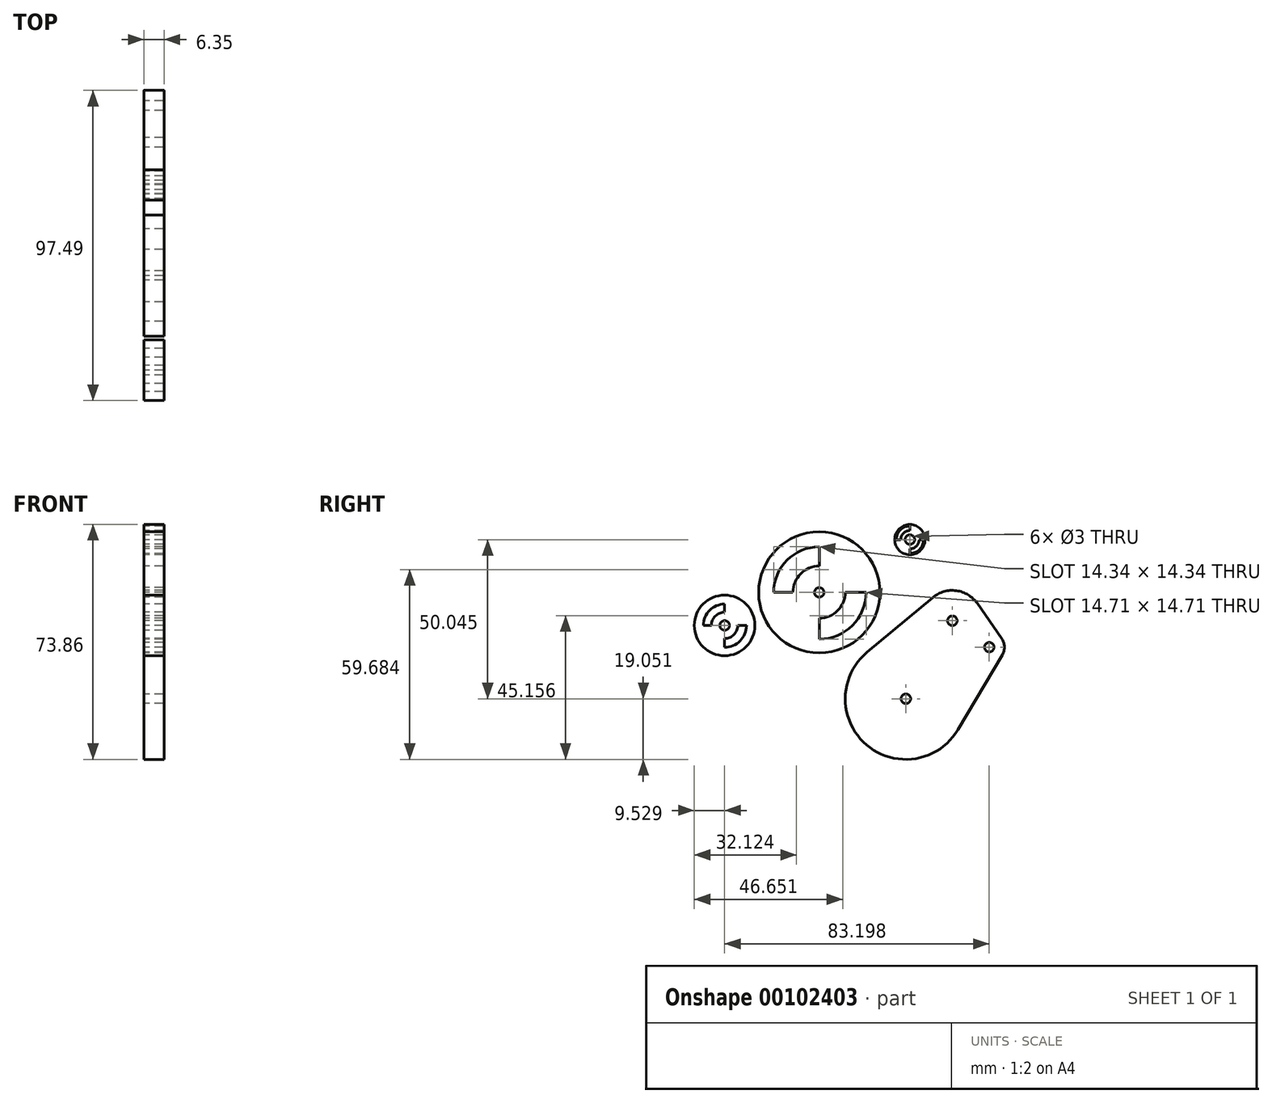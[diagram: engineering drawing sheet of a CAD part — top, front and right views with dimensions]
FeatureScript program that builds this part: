
annotation { "Feature Type Name" : "Feature", "Feature Type Description" : "" }
export const myFeature = defineFeature(function(context is Context, id is Id, definition is map)
    precondition{}
    {
        {
            var Q0;
            Q0=qCreatedBy(makeId("Right.planeOp"),FACE);
            var sketch = newSketch(context, id + "F0", { "sketchPlane" : qUnion([Q0])});
            skArc(sketch, "E0", {"start": v(-7.06, 29.74) * mm, "mid": v(-6.4, 32.34) * mm, "end": v(-7.25, 34.9) * mm});
            skArc(sketch, "E1", {"start": v(-49.56, 30.58) * mm, "mid": v(-49.72, 1.44) * mm, "end": v(-20.98, 6.23) * mm});
            skArc(sketch, "E2", {"start": v(-14.94, 45.94) * mm, "mid": v(-21.49, 49.94) * mm, "end": v(-28.86, 47.82) * mm});
            skCircle(sketch, "E3", {"center": v(-94.35, 39) * mm, "radius": 9.53 * mm});
            skCircle(sketch, "E4", {"center": v(-64.59, 49.4) * mm, "radius": 19.05 * mm});
            skCircle(sketch, "E5", {"center": v(-36.1, 65.99) * mm, "radius": 4.76 * mm});
            skLineSegment(sketch, "E6", {"start": v(-14.94, 45.94) * mm, "end": v(-7.25, 34.9) * mm});
            skLineSegment(sketch, "E7", {"start": v(-20.98, 6.23) * mm, "end": v(-7.06, 29.74) * mm});
            skLineSegment(sketch, "E8", {"start": v(-49.56, 30.58) * mm, "end": v(-28.86, 47.82) * mm});
            skPoint(sketch, "E9.orphan", {"position": v(0, 71.85) * mm});
            skCircle(sketch, "E10", {"center": v(-64.59, 49.4) * mm, "radius": 1.5 * mm});
            skCircle(sketch, "E11", {"center": v(-36.1, 65.99) * mm, "radius": 1.5 * mm});
            skCircle(sketch, "E12", {"center": v(-94.35, 39) * mm, "radius": 1.5 * mm});
            skCircle(sketch, "E13", {"center": v(-37.37, 15.94) * mm, "radius": 1.5 * mm});
            skCircle(sketch, "E14", {"center": v(-22.76, 40.5) * mm, "radius": 1.5 * mm});
            skCircle(sketch, "E15", {"center": v(-11.15, 32.17) * mm, "radius": 1.5 * mm});
            skPoint(sketch, "E16", {"position": v(-32.2, 38.2) * mm});
            skPoint(sketch, "E17", {"position": v(-15.89, 21.9) * mm});
            skArc(sketch, "E18", {"start": v(-64.59, 41.26) * mm, "mid": v(-58.83, 43.64) * mm, "end": v(-56.44, 49.4) * mm});
            skArc(sketch, "E19", {"start": v(-64.59, 34.69) * mm, "mid": v(-54.18, 39) * mm, "end": v(-49.87, 49.4) * mm});
            skLineSegment(sketch, "E20", {"start": v(-56.44, 49.4) * mm, "end": v(-49.87, 49.4) * mm});
            skLineSegment(sketch, "E21", {"start": v(-64.59, 41.26) * mm, "end": v(-64.59, 34.69) * mm});
            skArc(sketch, "E22", {"start": v(-72.88, 49.4) * mm, "mid": v(-70.45, 55.27) * mm, "end": v(-64.59, 57.7) * mm});
            skArc(sketch, "E23", {"start": v(-78.93, 49.4) * mm, "mid": v(-74.73, 59.54) * mm, "end": v(-64.59, 63.74) * mm});
            skLineSegment(sketch, "E24", {"start": v(-64.59, 63.74) * mm, "end": v(-64.59, 57.7) * mm});
            skLineSegment(sketch, "E25", {"start": v(-72.88, 49.4) * mm, "end": v(-78.93, 49.4) * mm});
            skArc(sketch, "E26", {"start": v(-94.35, 32.13) * mm, "mid": v(-89.49, 34.15) * mm, "end": v(-87.47, 39) * mm});
            skArc(sketch, "E27", {"start": v(-94.35, 34.89) * mm, "mid": v(-91.44, 36.1) * mm, "end": v(-90.23, 39) * mm});
            skArc(sketch, "E28", {"start": v(-101.06, 39) * mm, "mid": v(-99.1, 43.76) * mm, "end": v(-94.35, 45.72) * mm});
            skArc(sketch, "E29", {"start": v(-98.5, 39) * mm, "mid": v(-97.29, 41.95) * mm, "end": v(-94.35, 43.16) * mm});
            skLineSegment(sketch, "E30", {"start": v(-94.35, 45.72) * mm, "end": v(-94.35, 43.16) * mm});
            skLineSegment(sketch, "E31", {"start": v(-101.06, 39) * mm, "end": v(-98.5, 39) * mm});
            skLineSegment(sketch, "E32", {"start": v(-90.23, 39) * mm, "end": v(-87.47, 39) * mm});
            skLineSegment(sketch, "E33", {"start": v(-94.35, 34.89) * mm, "end": v(-94.35, 32.13) * mm});
            skArc(sketch, "E34", {"start": v(-36.1, 63.1) * mm, "mid": v(-34.06, 63.94) * mm, "end": v(-33.21, 65.99) * mm});
            skArc(sketch, "E35", {"start": v(-38.96, 65.99) * mm, "mid": v(-38.13, 68) * mm, "end": v(-36.1, 68.85) * mm});
            skArc(sketch, "E36", {"start": v(-36.1, 61.66) * mm, "mid": v(-33.05, 62.93) * mm, "end": v(-31.78, 65.99) * mm});
            skArc(sketch, "E37", {"start": v(-40.4, 65.99) * mm, "mid": v(-39.14, 69.02) * mm, "end": v(-36.1, 70.27) * mm});
            skLineSegment(sketch, "E38", {"start": v(-36.1, 70.27) * mm, "end": v(-36.1, 68.85) * mm});
            skLineSegment(sketch, "E39", {"start": v(-40.4, 65.99) * mm, "end": v(-38.96, 65.99) * mm});
            skLineSegment(sketch, "E40", {"start": v(-36.1, 63.1) * mm, "end": v(-36.1, 61.66) * mm});
            skLineSegment(sketch, "E41", {"start": v(-33.21, 65.99) * mm, "end": v(-31.78, 65.99) * mm});
            skSolve(sketch);
        }
        {
            var Q0;
            Q0=qSketchRegion(id+"F0",true);
            extrude(context, id + "F1", {"entities" : qUnion([Q0]), "depth" : 6.35 * mm});
        }
    });
